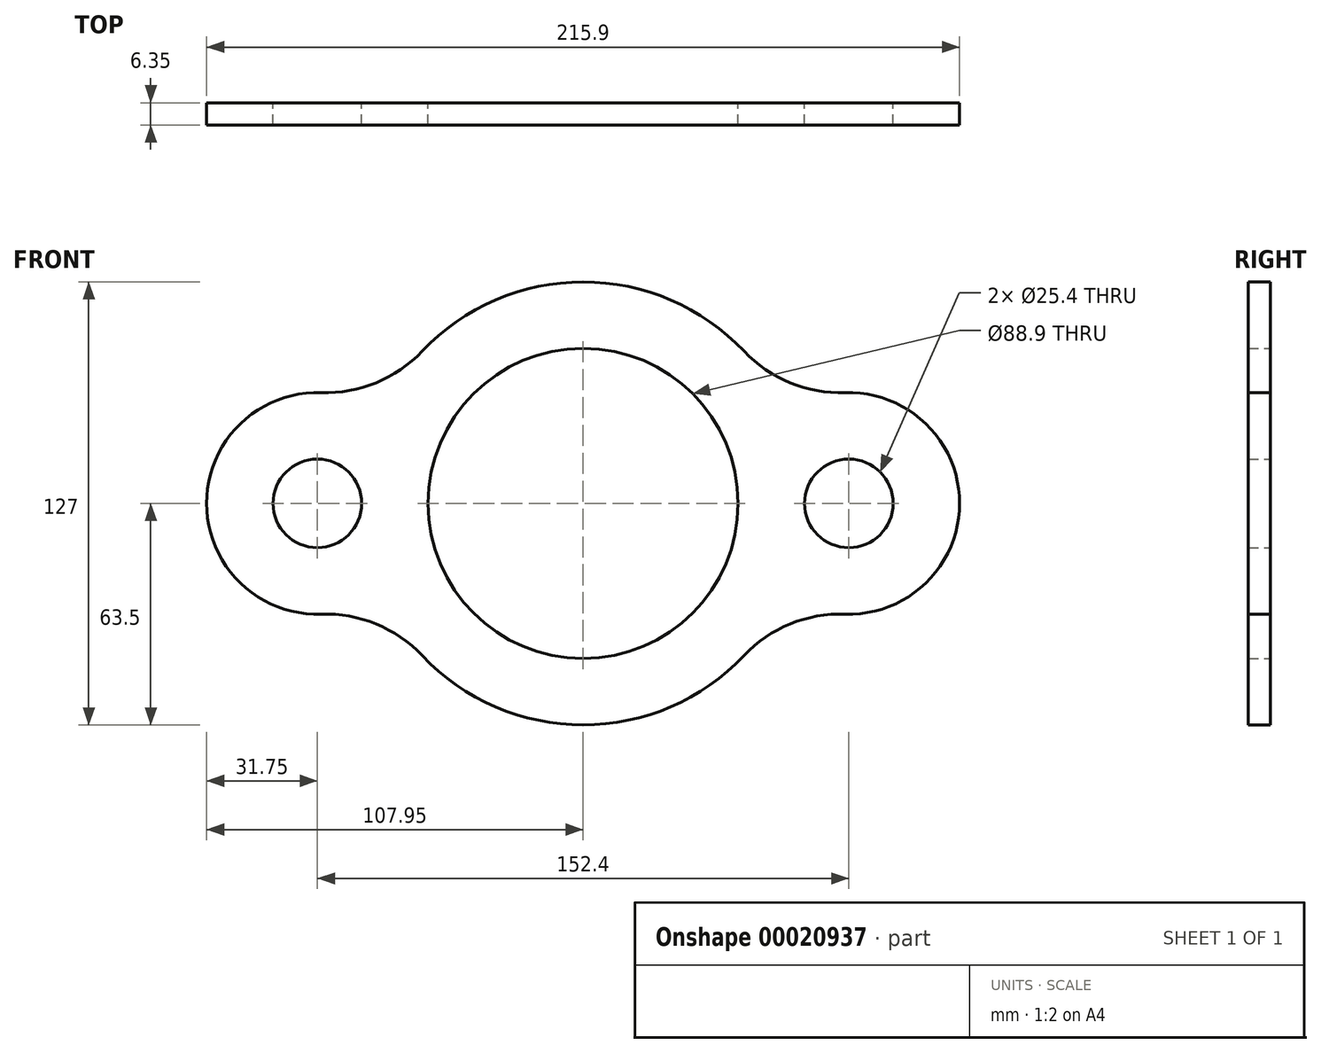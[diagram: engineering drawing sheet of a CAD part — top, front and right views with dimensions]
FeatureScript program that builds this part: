
annotation { "Feature Type Name" : "Feature", "Feature Type Description" : "" }
export const myFeature = defineFeature(function(context is Context, id is Id, definition is map)
    precondition{}
    {
        {
            var Q0;
            Q0=qCreatedBy(makeId("Front.planeOp"),FACE);
            var sketch = newSketch(context, id + "F0", { "sketchPlane" : qUnion([Q0])});
            skCircle(sketch, "E0", {"center": v(0, 0) * mm, "radius": 44.45 * mm});
            skArc(sketch, "E1", {"start": v(-46.14, -43.63) * mm, "mid": v(0, -63.5) * mm, "end": v(46.14, -43.63) * mm});
            skCircle(sketch, "E2", {"center": v(-76.2, 0) * mm, "radius": 12.7 * mm});
            skArc(sketch, "E3", {"start": v(-75.12, 31.73) * mm, "mid": v(-107.95, 0) * mm, "end": v(-75.12, -31.73) * mm});
            skCircle(sketch, "E4", {"center": v(76.2, 0) * mm, "radius": 12.7 * mm});
            skArc(sketch, "E5", {"start": v(75.12, -31.73) * mm, "mid": v(107.95, 0) * mm, "end": v(75.12, 31.73) * mm});
            skArc(sketch, "E6.trimOffspring", {"start": v(46.14, 43.63) * mm, "mid": v(0, 63.5) * mm, "end": v(-46.14, 43.63) * mm});
            skPoint(sketch, "E7.visualSharp", {"position": v(-57.94, 25.98) * mm});
            skArc(sketch, "E7.filletArc", {"start": v(-75.12, 31.73) * mm, "mid": v(-59.35, 34.56) * mm, "end": v(-46.14, 43.63) * mm});
            skPoint(sketch, "E8.visualSharp", {"position": v(57.94, 25.98) * mm});
            skArc(sketch, "E8.filletArc", {"start": v(46.14, 43.63) * mm, "mid": v(59.35, 34.56) * mm, "end": v(75.12, 31.73) * mm});
            skPoint(sketch, "E9.visualSharp", {"position": v(-57.94, -25.98) * mm});
            skArc(sketch, "E9.filletArc", {"start": v(-46.14, -43.63) * mm, "mid": v(-59.35, -34.56) * mm, "end": v(-75.12, -31.73) * mm});
            skPoint(sketch, "E10.visualSharp", {"position": v(57.94, -25.98) * mm});
            skArc(sketch, "E10.filletArc", {"start": v(75.12, -31.73) * mm, "mid": v(59.35, -34.56) * mm, "end": v(46.14, -43.63) * mm});
            skSolve(sketch);
        }
        {
            var Q0;
            Q0=makeQuery(id+"F0.imprint","IMPRINT",FACE,{"disambiguationData":[TD([[makeQuery(id+"F0.imprint","IMPRINT",EDGE,{"derivedFrom":sQuery(id+"F0.wireOp",EDGE,"E1")}),1.0]])]});
            extrude(context, id + "F1", {"entities" : qUnion([Q0]), "depth" : 6.35 * mm});
        }
    });
